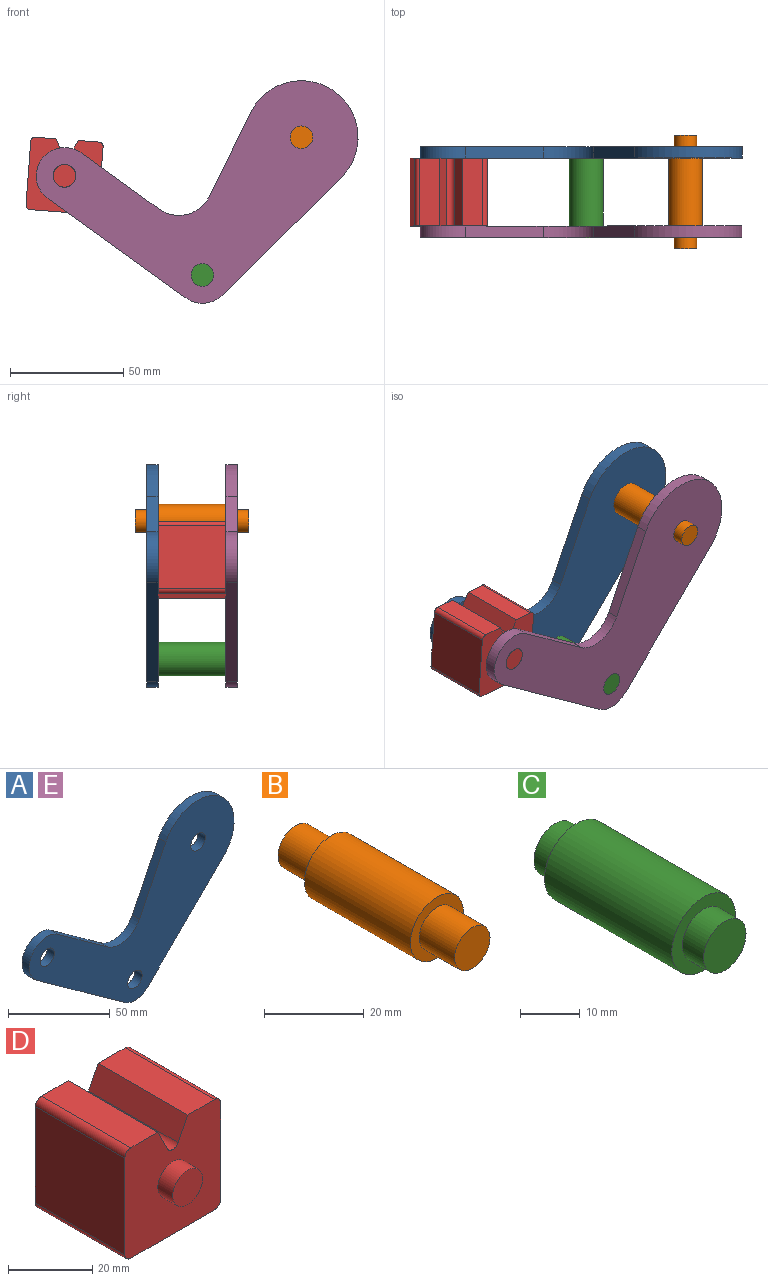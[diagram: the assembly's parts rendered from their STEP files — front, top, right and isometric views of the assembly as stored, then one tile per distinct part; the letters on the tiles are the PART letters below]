
ASSEMBLY  parts=5 mates=4
PART A: 13 faces, bbox 142.2x5x98.4 mm
  f0: plane 52.61x51.97mm, normal (0.7,0,-0.71), area 369.8mm2, adj f1,f9,f11,f12
  f1: cylinder r=25mm len=47.44mm, axis (0,-1,0), area 434.6mm2, adj f0,f2,f11,f12
  f2: plane 37.17x18.26mm, normal (-0.9,0,0.44), area 207.1mm2, adj f1,f3,f11,f12
  f3: cylinder r=15mm len=22.23mm, axis (0,-1,0), area 130.4mm2, adj f2,f4,f11,f12
  f4: plane 34.46x24.81mm, normal (0.58,0,0.81), area 212.3mm2, adj f3,f5,f11,f12
  f5: cylinder r=12.5mm len=22.64mm, axis (0,-1,0), area 196.3mm2, adj f4,f6,f11,f12
  f6: plane 60.86x43.82mm, normal (-0.58,0,-0.81), area 375mm2, adj f5,f9,f11,f12
  f7: cylinder r=5mm len=10mm, axis (0,-1,0), area 157.1mm2, adj f11,f12
  f8: cylinder r=5mm len=10mm, axis (0,-1,0), area 157.1mm2, adj f11,f12
  f9: cylinder r=12.5mm len=16.09mm, axis (0,-1,0), area 87.7mm2, adj f0,f6,f11,f12
  f10: cylinder r=5mm len=10mm, axis (0,-1,0), area 157.1mm2, adj f11,f12
  f11: plane 142.19x98.36mm, normal (0,1,0), area 5739.8mm2, adj f0,f1,f2,f3,f4,f5,f6,f7
  f12: plane 142.19x98.36mm, normal (0,-1,0), area 5739.8mm2, adj f0,f1,f2,f3,f4,f5,f6,f7
PART B: 7 faces, bbox 15x50x15 mm
  f0: cylinder r=7.5mm len=30mm, axis (0,-1,0), area 1413.7mm2, adj f2,f5
  f1: cylinder r=5mm len=10mm, axis (0,1,0), area 314.2mm2, adj f2,f3
  f2: plane 15x15mm, normal (0,-1,0), area 98.2mm2, adj f0,f1
  f3: plane 10x10mm, normal (0,-1,0), area 78.5mm2, adj f1
  f4: cylinder r=5mm len=10mm, axis (0,-1,0), area 314.2mm2, adj f5,f6
  f5: plane 15x15mm, normal (0,1,0), area 98.2mm2, adj f0,f4
  f6: plane 10x10mm, normal (0,1,0), area 78.5mm2, adj f4
PART C: 7 faces, bbox 15x40x15 mm
  f0: cylinder r=7.5mm len=30mm, axis (0,-1,0), area 1413.7mm2, adj f2,f5
  f1: cylinder r=5mm len=10mm, axis (0,-1,0), area 157.1mm2, adj f2,f3
  f2: plane 15x15mm, normal (0,-1,0), area 98.2mm2, adj f0,f1
  f3: plane 10x10mm, normal (0,-1,0), area 78.5mm2, adj f1
  f4: cylinder r=5mm len=10mm, axis (0,1,0), area 157.1mm2, adj f5,f6
  f5: plane 15x15mm, normal (0,1,0), area 98.2mm2, adj f0,f4
  f6: plane 10x10mm, normal (0,1,0), area 78.5mm2, adj f4
PART D: 18 faces, bbox 32.1x40x32.1 mm
  f0: plane 30x6.42mm, normal (0.89,0,0.45), area 215.4mm2, adj f4,f6,f10,f13
  f1: plane 30x6.42mm, normal (-0.89,0,0.45), area 215.4mm2, adj f2,f4,f10,f13
  f2: plane 30x9.04mm, normal (0,0,1), area 271.2mm2, adj f1,f4,f10,f14
  f3: plane 30x28.08mm, normal (1,0,0), area 842.3mm2, adj f4,f10,f14,f15
  f4: plane 32.08x32.08mm, normal (0,-1,0), area 900.6mm2, adj f0,f1,f2,f3,f5,f6,f7,f9
  f5: plane 30x28.08mm, normal (0,0,-1), area 842.3mm2, adj f4,f10,f15,f16
  f6: plane 30x9.04mm, normal (0,0,1), area 271.2mm2, adj f0,f4,f10,f17
  f7: plane 30x28.08mm, normal (-1,0,0), area 842.3mm2, adj f4,f10,f16,f17
  f8: plane 10x10mm, normal (0,-1,0), area 78.5mm2, adj f9
  f9: cylinder r=5mm len=10mm, axis (0,1,0), area 157.1mm2, adj f4,f8
  f10: plane 32.08x32.08mm, normal (0,1,0), area 900.6mm2, adj f0,f1,f2,f3,f5,f6,f7,f12
  f11: plane 10x10mm, normal (0,1,0), area 78.5mm2, adj f12
  f12: cylinder r=5mm len=10mm, axis (0,-1,0), area 157.1mm2, adj f10,f11
  f13: cylinder r=2mm len=30mm, axis (0,1,0), area 132.9mm2, adj f0,f1,f4,f10
  f14: cylinder r=2mm len=30mm, axis (0,1,0), area 94.2mm2, adj f2,f3,f4,f10
  f15: cylinder r=2mm len=30mm, axis (0,-1,0), area 94.2mm2, adj f3,f4,f5,f10
  f16: cylinder r=2mm len=30mm, axis (0,1,0), area 94.2mm2, adj f4,f5,f7,f10
  f17: cylinder r=2mm len=30mm, axis (0,-1,0), area 94.2mm2, adj f4,f6,f7,f10
PART E: same geometry as A
PLACE A t=(0,15,0)mm
PLACE B t=(0,-20,0)mm fixed
PLACE C t=(0,-20,0)mm
PLACE D rot(axis=(0,1,0),4.3deg) t=(0.98,-20,-7.83)mm
PLACE E t=(0,-20,0)mm
MATE fastened C.f0 <-> E.f7  axis (0,-1,0) through (-43.82,-15,-60.86)mm
MATE fastened B.f0 <-> E.f1  axis (0,-1,0) through (0,-15,0)mm
MATE fastened C.f0 <-> A.f7  axis (0,1,0) through (-43.82,15,-60.86)mm
MATE revolute D.f9 <-> E.f5  axis (0,-1,0) through (-104.69,-15,-17.04)mm
